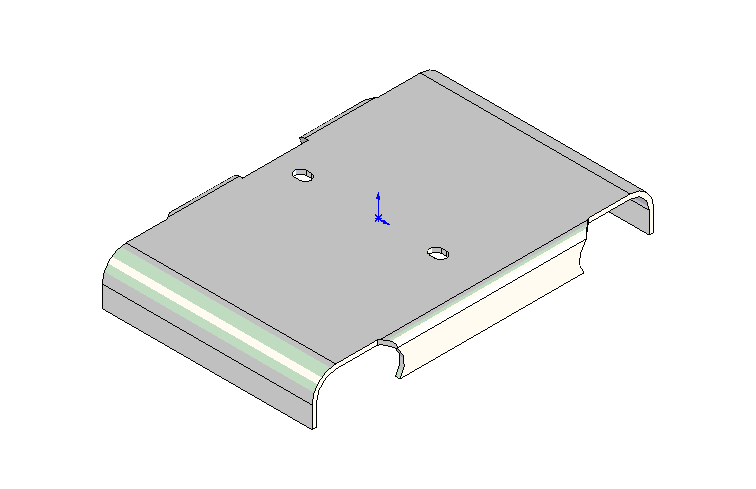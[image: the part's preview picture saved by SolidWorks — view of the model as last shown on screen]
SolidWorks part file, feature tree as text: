
SOLIDWORKS PART (.sldprt)
format: sldprt  version: not decoded by parser v0  size: 391,680 bytes
history: native  units: mm
features: cut_extrude x4, plane x3, fillet x2, material x1, sketch x1, extrude x1, shell x1 + 4 further entries (+10 scaffold rows collapsed)
feature tree (27):
  scaffold x10  (default folders/planes/origin — collapsed)
  material  "Matériau <non spécifié>"
  plane  "Plan de face"
  plane  "Plan de dessus"
  plane  "Plan de droite"
  sketch  "Esquisse1"  dims[D1=151.5mm D2=101.0mm]
  extrude  "Extrusion1"  Depth=20mm
  fillet  "Congé2"  Radius=10.5mm
  fillet  "Congé3"  Radius=3.5mm
  shell  "Coque1"  Thickness=2mm
  "Esquisse5"
  cut_extrude  "Enlèv. mat.-Extru.4"  [1 undecoded]
  "Esquisse2"
  cut_extrude  "Enlèv. mat.-Extru.1"  [1 undecoded]
  "Esquisse3"
  cut_extrude  "Enlèv. mat.-Extru.2"  Depth=5mm
  "Esquisse6"
  cut_extrude  "Enlèv. mat.-Extru.5"  [1 undecoded]
decode coverage: 6 of 9 modeling features carry decoded parameters; 4 rows unclassified (native names shown)
note: 3 parameter values undecoded
summary: no parameter record found for 3 features
note: suppression state not decoded; provenance and decode notes live in map.json
